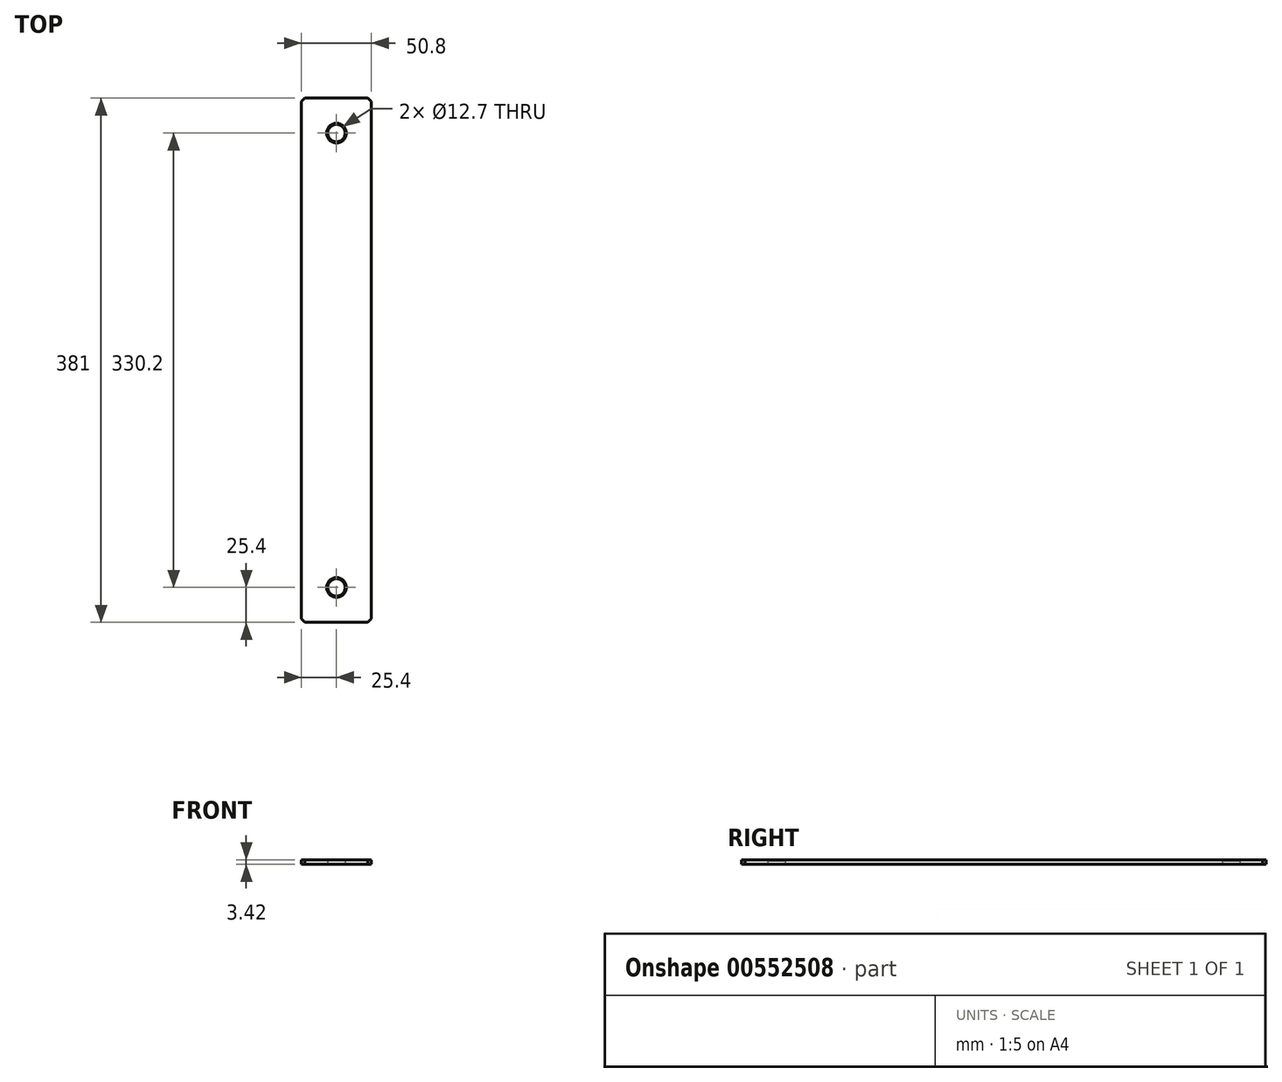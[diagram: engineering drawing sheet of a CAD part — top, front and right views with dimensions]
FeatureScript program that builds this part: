
annotation { "Feature Type Name" : "Feature", "Feature Type Description" : "" }
export const myFeature = defineFeature(function(context is Context, id is Id, definition is map)
    precondition{}
    {
        {
            var Q0;
            Q0=qCreatedBy(makeId("Top.planeOp"),FACE);
            var sketch = newSketch(context, id + "F0", { "sketchPlane" : qUnion([Q0])});
            skLineSegment(sketch, "E0.bottom", {"start": v(25.4, 190.5) * mm, "end": v(-25.4, 190.5) * mm});
            skLineSegment(sketch, "E0.top", {"start": v(25.4, -190.5) * mm, "end": v(-25.4, -190.5) * mm});
            skLineSegment(sketch, "E0.left", {"start": v(25.4, 190.5) * mm, "end": v(25.4, -190.5) * mm});
            skLineSegment(sketch, "E0.right", {"start": v(-25.4, 190.5) * mm, "end": v(-25.4, -190.5) * mm});
            skPoint(sketch, "E0.middle", {"position": v(0, 0) * mm});
            skCircle(sketch, "E1", {"center": v(0, 165.1) * mm, "radius": 6.35 * mm});
            skCircle(sketch, "E2", {"center": v(0, -165.1) * mm, "radius": 6.35 * mm});
            skSolve(sketch);
        }
        {
            var Q0;
            Q0=makeQuery(id+"F0.imprint","IMPRINT",FACE,{"disambiguationData":[TD([[makeQuery(id+"F0.imprint","IMPRINT",EDGE,{"derivedFrom":sQuery(id+"F0.wireOp",EDGE,"E0.bottom")}),1.0]])]});
            extrude(context, id + "F1", {"entities" : qUnion([Q0]), "depth" : 3.43 * mm, "offsetDistance" : 25.4 * mm, "symmetric" : true});
        }
        {
            var Q0;
            Q0=makeQuery(id+"F1.opExtrude","SWEPT_EDGE",EDGE,{"disambiguationData":[OSD([sQuery(id+"F0.wireOp",EDGE,"E0.top"),sQuery(id+"F0.wireOp",EDGE,"E0.left")])]});
            var Q1;
            Q1=makeQuery(id+"F1.opExtrude","SWEPT_EDGE",EDGE,{"disambiguationData":[OSD([sQuery(id+"F0.wireOp",EDGE,"E0.top"),sQuery(id+"F0.wireOp",EDGE,"E0.right")])]});
            var Q2;
            Q2=makeQuery(id+"F1.opExtrude","SWEPT_EDGE",EDGE,{"disambiguationData":[OSD([sQuery(id+"F0.wireOp",EDGE,"E0.bottom"),sQuery(id+"F0.wireOp",EDGE,"E0.right")])]});
            var Q3;
            Q3=makeQuery(id+"F1.opExtrude","SWEPT_EDGE",EDGE,{"disambiguationData":[OSD([sQuery(id+"F0.wireOp",EDGE,"E0.bottom"),sQuery(id+"F0.wireOp",EDGE,"E0.left")])]});
            chamfer(context, id + "F2", {"entities" : qUnion([Q0, Q1, Q2, Q3]), "width" : 2.54 * mm, "tangentPropagation" : true});
        }
        {
            var Q0;
            Q0=makeQuery(id+"F1.opExtrude","CAP_EDGE",EDGE,{"disambiguationData":[OSD([sQuery(id+"F0.wireOp",EDGE,"E2")])],"isStart":false});
            var Q1;
            Q1=makeQuery(id+"F1.opExtrude","CAP_EDGE",EDGE,{"disambiguationData":[OSD([sQuery(id+"F0.wireOp",EDGE,"E1")])],"isStart":false});
            chamfer(context, id + "F3", {"entities" : qUnion([Q0, Q1]), "width" : 0.79 * mm, "tangentPropagation" : true});
        }
    });
